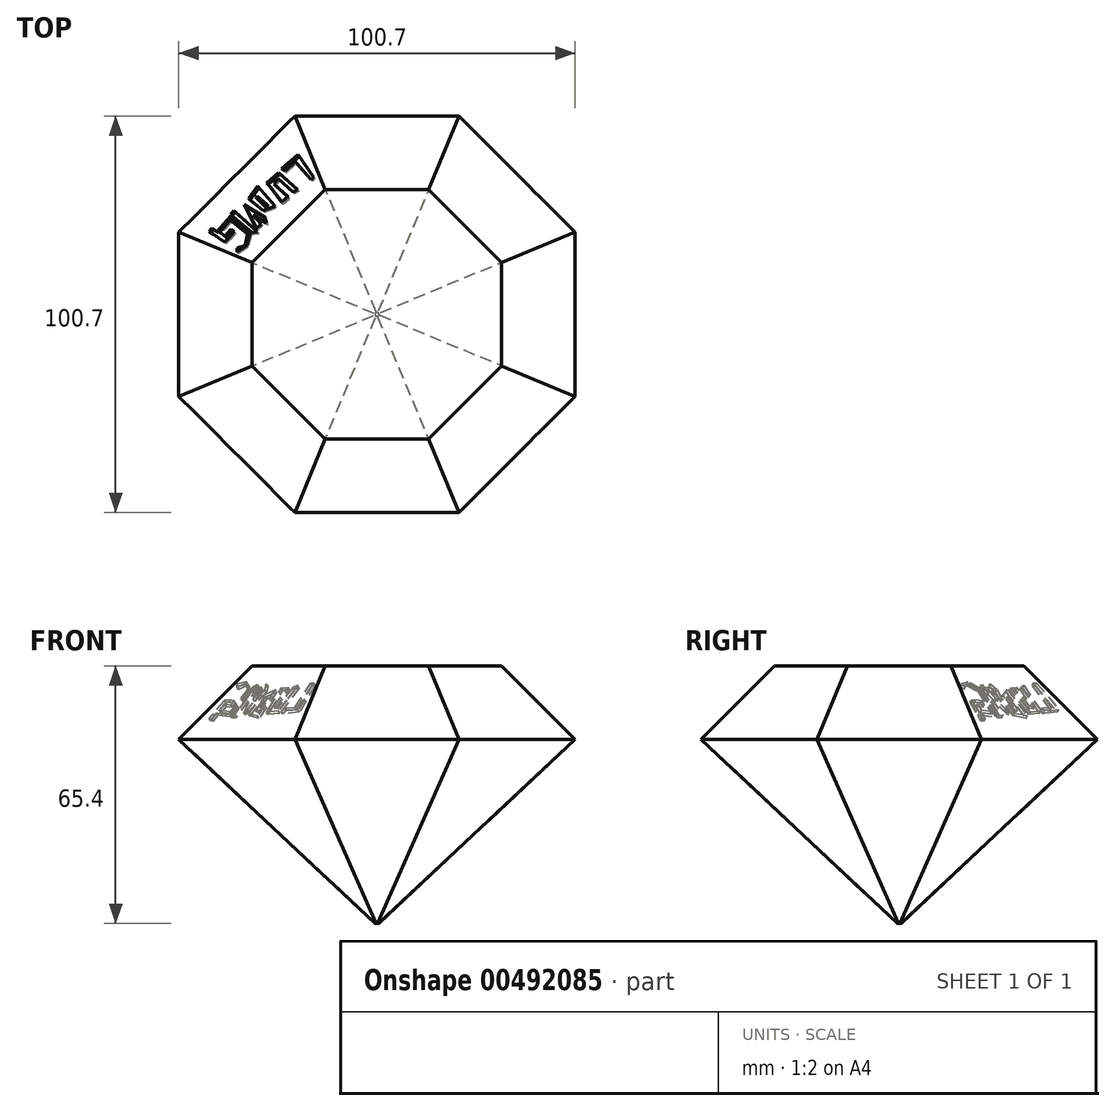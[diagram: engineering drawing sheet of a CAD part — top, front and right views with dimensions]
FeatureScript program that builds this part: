
annotation { "Feature Type Name" : "Feature", "Feature Type Description" : "" }
export const myFeature = defineFeature(function(context is Context, id is Id, definition is map)
    precondition{}
    {
        {
            var Q0;
            Q0=qCreatedBy(makeId("Top.planeOp"),FACE);
            var sketch = newSketch(context, id + "F0", { "sketchPlane" : qUnion([Q0])});
            skCircle(sketch, "E0", {"center": v(0, 0) * mm, "radius": 0.5 * mm});
            skSolve(sketch);
        }
        {
            var Q0;
            Q0=qCreatedBy(makeId("Top.planeOp"),FACE);
            cPlane(context, id + "F1", {"entities" : qUnion([Q0]), "cplaneType" : CPlaneType.OFFSET, "offset" : 48 * mm, "width" : 150 * mm, "height" : 150 * mm});
        }
        {
            var Q0;
            Q0=qCreatedBy(id+"F1.planeOp",FACE);
            var sketch = newSketch(context, id + "F2", { "sketchPlane" : qUnion([Q0])});
            skCircle(sketch, "E1.cCircle", {"center": v(0, 0) * mm, "radius": 51.69 * mm, "construction": true});
            skLineSegment(sketch, "E1.0", {"start": v(-21.41, 51.69) * mm, "end": v(21.41, 51.69) * mm});
            skLineSegment(sketch, "E1.1", {"start": v(21.41, 51.69) * mm, "end": v(51.69, 21.41) * mm});
            skLineSegment(sketch, "E1.2", {"start": v(51.69, 21.41) * mm, "end": v(51.69, -21.41) * mm});
            skLineSegment(sketch, "E1.3", {"start": v(51.69, -21.41) * mm, "end": v(21.41, -51.69) * mm});
            skLineSegment(sketch, "E1.4", {"start": v(21.41, -51.69) * mm, "end": v(-21.41, -51.69) * mm});
            skLineSegment(sketch, "E1.5", {"start": v(-21.41, -51.69) * mm, "end": v(-51.69, -21.41) * mm});
            skLineSegment(sketch, "E1.6", {"start": v(-51.69, -21.41) * mm, "end": v(-51.69, 21.41) * mm});
            skLineSegment(sketch, "E1.7", {"start": v(-51.69, 21.41) * mm, "end": v(-21.41, 51.69) * mm});
            skPoint(sketch, "E1.0.midPoint", {"position": v(0, 51.69) * mm});
            skSolve(sketch);
        }
        {
            var Q0;
            Q0=makeQuery(id+"F2.imprint","IMPRINT",FACE,{"disambiguationData":[TD([[makeQuery(id+"F2.imprint","IMPRINT",EDGE,{"derivedFrom":sQuery(id+"F2.wireOp",EDGE,"E1.0")}),-1.0]])]});
            var Q1;
            Q1=makeQuery(id+"F0.imprint","IMPRINT",FACE,{"disambiguationData":[TD([[makeQuery(id+"F0.imprint","IMPRINT",EDGE,{"derivedFrom":sQuery(id+"F0.wireOp",EDGE,"E0")}),1.0]])]});
            loft(context, id + "F3", {"sheetProfilesArray" : [{ "sheetProfileEntities" : qUnion([Q0]) }, { "sheetProfileEntities" : qUnion([Q1]) }]});
        }
        {
            var Q0;
            Q0=makeQuery(id+"F3.opLoft","CAP_FACE",FACE,{"disambiguationData":[OSD([makeQuery(id+"F2.imprint","IMPRINT",FACE,{"disambiguationData":[TD([[makeQuery(id+"F2.imprint","IMPRINT",EDGE,{"derivedFrom":sQuery(id+"F2.wireOp",EDGE,"E1.0")}),-1.0]])]})])],"isStart":true});
            extrude(context, id + "F4", {"entities" : qUnion([Q0]), "operationType" : NewBodyOperationType.ADD, "depth" : 17.4 * mm});
        }
        {
            var Q0;
            Q0=makeQuery(id+"F4.opExtrude","CAP_EDGE",EDGE,{"disambiguationData":[OSD([sQuery(id+"F2.wireOp",EDGE,"E1.3"),sQuery(id+"F2.wireOp",EDGE,"E1.4"),sQuery(id+"F2.wireOp",EDGE,"E1.5")])],"isStart":false});
            var Q1;
            Q1=makeQuery(id+"F4.opExtrude","CAP_EDGE",EDGE,{"disambiguationData":[OSD([sQuery(id+"F2.wireOp",EDGE,"E1.2"),sQuery(id+"F2.wireOp",EDGE,"E1.3"),sQuery(id+"F2.wireOp",EDGE,"E1.4")])],"isStart":false});
            var Q2;
            Q2=makeQuery(id+"F4.opExtrude","CAP_EDGE",EDGE,{"disambiguationData":[OSD([sQuery(id+"F2.wireOp",EDGE,"E1.4"),sQuery(id+"F2.wireOp",EDGE,"E1.5"),sQuery(id+"F2.wireOp",EDGE,"E1.6")])],"isStart":false});
            var Q3;
            Q3=makeQuery(id+"F4.opExtrude","CAP_EDGE",EDGE,{"disambiguationData":[OSD([sQuery(id+"F2.wireOp",EDGE,"E1.5"),sQuery(id+"F2.wireOp",EDGE,"E1.6"),sQuery(id+"F2.wireOp",EDGE,"E1.7")])],"isStart":false});
            var Q4;
            Q4=makeQuery(id+"F4.opExtrude","CAP_EDGE",EDGE,{"disambiguationData":[OSD([sQuery(id+"F2.wireOp",EDGE,"E1.0"),sQuery(id+"F2.wireOp",EDGE,"E1.6"),sQuery(id+"F2.wireOp",EDGE,"E1.7")])],"isStart":false});
            var Q5;
            Q5=makeQuery(id+"F4.opExtrude","CAP_EDGE",EDGE,{"disambiguationData":[OSD([sQuery(id+"F2.wireOp",EDGE,"E1.0"),sQuery(id+"F2.wireOp",EDGE,"E1.1"),sQuery(id+"F2.wireOp",EDGE,"E1.7")])],"isStart":false});
            var Q6;
            Q6=makeQuery(id+"F4.opExtrude","CAP_EDGE",EDGE,{"disambiguationData":[OSD([sQuery(id+"F2.wireOp",EDGE,"E1.0"),sQuery(id+"F2.wireOp",EDGE,"E1.1"),sQuery(id+"F2.wireOp",EDGE,"E1.2")])],"isStart":false});
            var Q7;
            Q7=makeQuery(id+"F4.opExtrude","CAP_EDGE",EDGE,{"disambiguationData":[OSD([sQuery(id+"F2.wireOp",EDGE,"E1.1"),sQuery(id+"F2.wireOp",EDGE,"E1.2"),sQuery(id+"F2.wireOp",EDGE,"E1.3")])],"isStart":false});
            chamfer(context, id + "F5", {"entities" : qUnion([Q0, Q1, Q2, Q3, Q4, Q5, Q6, Q7]), "width" : 20 * mm, "tangentPropagation" : true});
        }
        {
            var Q0;
            Q0=makeQuery(id+"F5.opChamfer","BLEND_FACE",FACE,{"disambiguationData":[OSD([sQuery(id+"F2.wireOp",EDGE,"E1.0"),sQuery(id+"F2.wireOp",EDGE,"E1.6"),sQuery(id+"F2.wireOp",EDGE,"E1.7")])]});
            var sketch = newSketch(context, id + "F6", { "sketchPlane" : qUnion([Q0])});
            skLineSegment(sketch, "E2", {"start": v(8.03, -4.83) * mm, "end": v(11.68, -11.32) * mm});
            skLineSegment(sketch, "E3", {"start": v(11.68, -11.32) * mm, "end": v(13.56, -10.26) * mm});
            skLineSegment(sketch, "E4", {"start": v(9.77, -11.88) * mm, "end": v(4.64, -3.86) * mm});
            skLineSegment(sketch, "E5", {"start": v(4.64, -3.86) * mm, "end": v(1.95, -6.8) * mm});
            skLineSegment(sketch, "E6", {"start": v(1.95, -6.8) * mm, "end": v(6.17, -11.88) * mm});
            skLineSegment(sketch, "E7", {"start": v(6.17, -11.88) * mm, "end": v(9.77, -11.88) * mm});
            skLineSegment(sketch, "E8", {"start": v(4.54, -6.8) * mm, "end": v(7.36, -10.55) * mm});
            skLineSegment(sketch, "E9", {"start": v(7.36, -10.55) * mm, "end": v(6.82, -10.85) * mm});
            skLineSegment(sketch, "E10", {"start": v(6.82, -10.85) * mm, "end": v(4.06, -7.04) * mm});
            skLineSegment(sketch, "E11", {"start": v(4.06, -7.04) * mm, "end": v(4.54, -6.8) * mm});
            skLineSegment(sketch, "E12", {"start": v(6.72, -14.1) * mm, "end": v(0.7, -8.07) * mm});
            skPoint(sketch, "E12.endSnap0", {"position": v(9.86, -8.07) * mm});
            skLineSegment(sketch, "E13", {"start": v(0.7, -8.07) * mm, "end": v(4.22, -16.85) * mm});
            skLineSegment(sketch, "E14", {"start": v(4.22, -16.85) * mm, "end": v(5.7, -15.9) * mm});
            skLineSegment(sketch, "E15", {"start": v(5.7, -15.9) * mm, "end": v(3.38, -12.28) * mm});
            skLineSegment(sketch, "E16", {"start": v(3.38, -12.28) * mm, "end": v(7.19, -16.26) * mm});
            skLineSegment(sketch, "E17", {"start": v(7.19, -16.26) * mm, "end": v(6.72, -14.1) * mm});
            skLineSegment(sketch, "E18", {"start": v(4.54, -17.96) * mm, "end": v(-2.36, -8.98) * mm});
            skLineSegment(sketch, "E19", {"start": v(2.94, -17.65) * mm, "end": v(4.54, -17.96) * mm});
            skLineSegment(sketch, "E20", {"start": v(-1.38, -20.9) * mm, "end": v(-1.38, -22.16) * mm});
            skLineSegment(sketch, "E21", {"start": v(-1.38, -20.9) * mm, "end": v(0.95, -20.9) * mm});
            skLineSegment(sketch, "E22", {"start": v(0.95, -20.9) * mm, "end": v(1.75, -17.65) * mm});
            skLineSegment(sketch, "E23", {"start": v(1.75, -17.65) * mm, "end": v(-3.51, -11.55) * mm});
            skLineSegment(sketch, "E24", {"start": v(-3.51, -11.55) * mm, "end": v(-6.47, -14.1) * mm});
            skLineSegment(sketch, "E25", {"start": v(-6.47, -14.1) * mm, "end": v(-4.92, -15.9) * mm});
            skLineSegment(sketch, "E26", {"start": v(-4.92, -15.9) * mm, "end": v(-3.2, -14.4) * mm});
            skLineSegment(sketch, "E27", {"start": v(-3.2, -14.4) * mm, "end": v(-2.25, -15.5) * mm});
            skLineSegment(sketch, "E28", {"start": v(-2.25, -15.5) * mm, "end": v(-3.7, -16.82) * mm});
            skLineSegment(sketch, "E29", {"start": v(-3.7, -16.82) * mm, "end": v(-5.13, -17.73) * mm});
            skLineSegment(sketch, "E30", {"start": v(-5.13, -17.73) * mm, "end": v(-8.48, -14.1) * mm});
            skLineSegment(sketch, "E31", {"start": v(-8.48, -14.1) * mm, "end": v(-9.58, -12.88) * mm});
            skLineSegment(sketch, "E32", {"start": v(-9.58, -12.88) * mm, "end": v(-8.72, -12.1) * mm});
            skLineSegment(sketch, "E33", {"start": v(-8.72, -12.1) * mm, "end": v(-7.24, -13.75) * mm});
            skLineSegment(sketch, "E34", {"start": v(-7.24, -13.75) * mm, "end": v(-3.38, -10.26) * mm});
            skLineSegment(sketch, "E35", {"start": v(-3.38, -10.26) * mm, "end": v(2.43, -17.65) * mm});
            skLineSegment(sketch, "E36", {"start": v(2.43, -17.65) * mm, "end": v(1.33, -21.13) * mm});
            skLineSegment(sketch, "E37", {"start": v(1.33, -21.13) * mm, "end": v(-1.38, -22.16) * mm});
            skLineSegment(sketch, "E38", {"start": v(-2.36, -8.98) * mm, "end": v(-3.36, -9.75) * mm});
            skLineSegment(sketch, "E39", {"start": v(-3.36, -9.75) * mm, "end": v(2.94, -17.65) * mm});
            skLineSegment(sketch, "E40", {"start": v(21.05, -6.76) * mm, "end": v(16.5, 1.81) * mm});
            skLineSegment(sketch, "E41", {"start": v(16.5, 1.81) * mm, "end": v(11.68, -0.9) * mm});
            skLineSegment(sketch, "E42", {"start": v(11.68, -0.9) * mm, "end": v(12.63, -1.89) * mm});
            skLineSegment(sketch, "E43", {"start": v(12.63, -1.89) * mm, "end": v(15.58, 0) * mm});
            skLineSegment(sketch, "E44", {"start": v(15.58, 0) * mm, "end": v(20.26, -7.32) * mm});
            skLineSegment(sketch, "E45", {"start": v(20.26, -7.32) * mm, "end": v(21.05, -6.76) * mm});
            skLineSegment(sketch, "E46", {"start": v(16.35, -8.98) * mm, "end": v(10.76, -1.7) * mm});
            skLineSegment(sketch, "E47", {"start": v(10.76, -1.7) * mm, "end": v(7.19, -3.71) * mm});
            skLineSegment(sketch, "E48", {"start": v(7.19, -3.71) * mm, "end": v(8.03, -4.83) * mm});
            skLineSegment(sketch, "E49", {"start": v(16.35, -8.98) * mm, "end": v(14.96, -9.27) * mm});
            skLineSegment(sketch, "E50", {"start": v(14.96, -9.27) * mm, "end": v(10.63, -3.65) * mm});
            skLineSegment(sketch, "E51", {"start": v(10.63, -3.65) * mm, "end": v(9.4, -4.83) * mm});
            skLineSegment(sketch, "E52", {"start": v(9.4, -4.83) * mm, "end": v(13.56, -10.26) * mm});
            skSolve(sketch);
        }
        {
            var Q0;
            Q0=makeQuery(id+"F6.imprint","IMPRINT",FACE,{"disambiguationData":[TD([[makeQuery(id+"F6.imprint","IMPRINT",EDGE,{"derivedFrom":sQuery(id+"F6.wireOp",EDGE,"E40")}),1.0]])]});
            var Q1;
            Q1=makeQuery(id+"F6.imprint","IMPRINT",FACE,{"disambiguationData":[TD([[makeQuery(id+"F6.imprint","IMPRINT",EDGE,{"derivedFrom":sQuery(id+"F6.wireOp",EDGE,"E2")}),1.0]])]});
            var Q2;
            Q2=makeQuery(id+"F6.imprint","IMPRINT",FACE,{"disambiguationData":[TD([[makeQuery(id+"F6.imprint","IMPRINT",EDGE,{"derivedFrom":sQuery(id+"F6.wireOp",EDGE,"E4")}),1.0]])]});
            var Q3;
            Q3=makeQuery(id+"F6.imprint","IMPRINT",FACE,{"disambiguationData":[TD([[makeQuery(id+"F6.imprint","IMPRINT",EDGE,{"derivedFrom":sQuery(id+"F6.wireOp",EDGE,"E12")}),1.0]])]});
            var Q4;
            Q4=makeQuery(id+"F6.imprint","IMPRINT",FACE,{"disambiguationData":[TD([[makeQuery(id+"F6.imprint","IMPRINT",EDGE,{"derivedFrom":sQuery(id+"F6.wireOp",EDGE,"E18")}),1.0]])]});
            var Q5;
            Q5=makeQuery(id+"F6.imprint","IMPRINT",FACE,{"disambiguationData":[TD([[makeQuery(id+"F6.imprint","IMPRINT",EDGE,{"derivedFrom":sQuery(id+"F6.wireOp",EDGE,"E20")}),1.0]])]});
            extrude(context, id + "F7", {"entities" : qUnion([Q0, Q1, Q2, Q3, Q4, Q5]), "operationType" : NewBodyOperationType.REMOVE, "oppositeDirection" : true, "depth" : 0.8 * mm});
        }
    });
